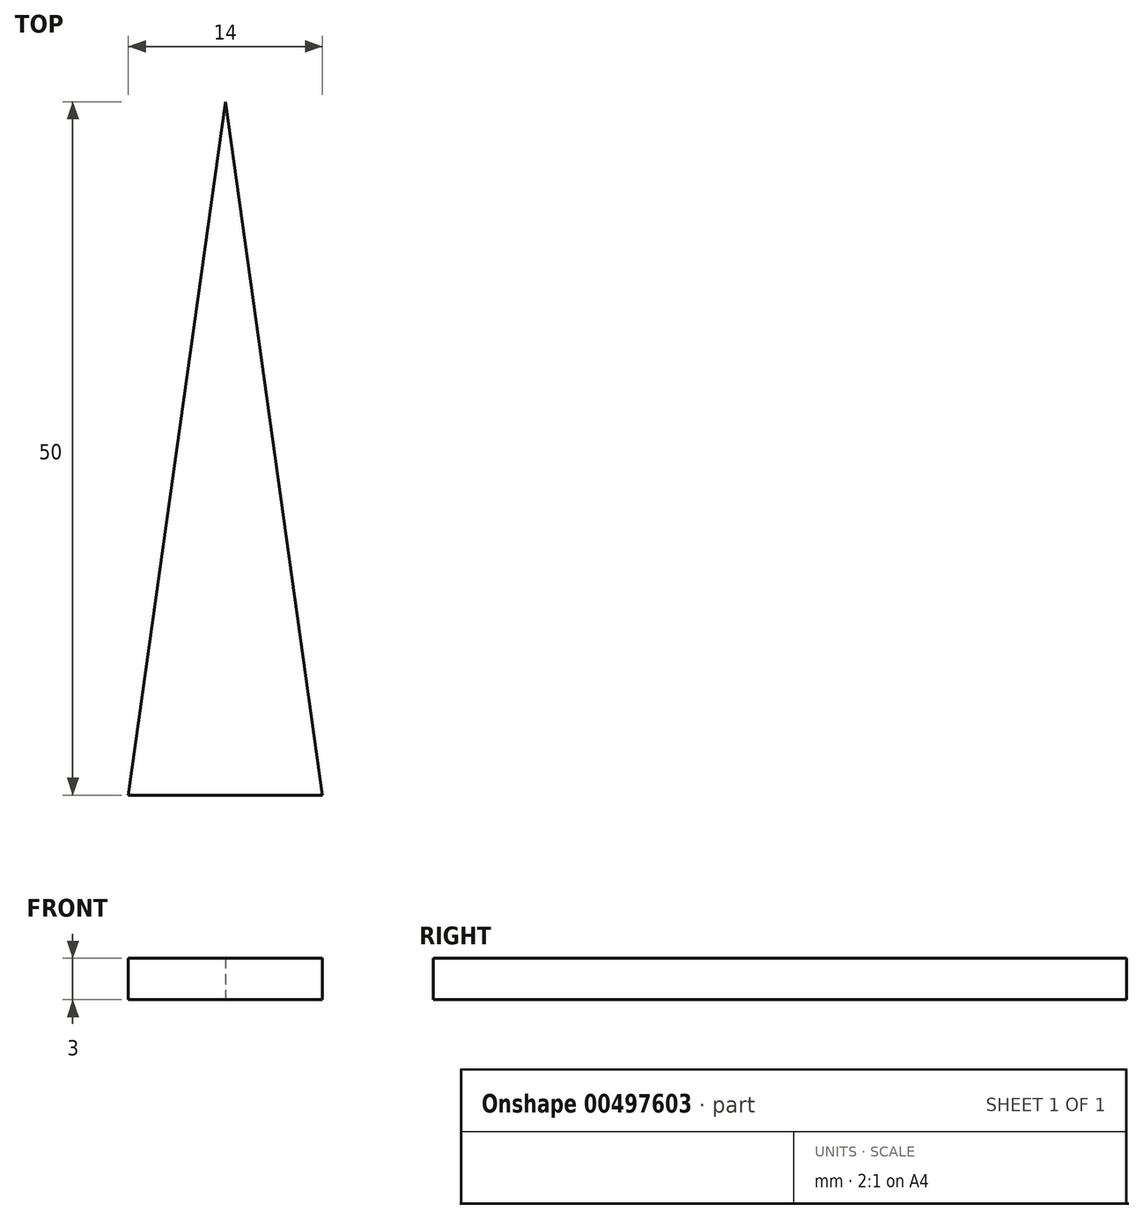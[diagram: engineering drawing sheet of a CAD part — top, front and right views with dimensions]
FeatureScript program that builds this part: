
annotation { "Feature Type Name" : "Feature", "Feature Type Description" : "" }
export const myFeature = defineFeature(function(context is Context, id is Id, definition is map)
    precondition{}
    {
        {
            var Q0;
            Q0=qCreatedBy(makeId("Top.planeOp"),FACE);
            var sketch = newSketch(context, id + "F0", { "sketchPlane" : qUnion([Q0])});
            skLineSegment(sketch, "E0", {"start": v(0, 0) * mm, "end": v(-7, -50) * mm});
            skLineSegment(sketch, "E1", {"start": v(-7, -50) * mm, "end": v(7, -50) * mm});
            skLineSegment(sketch, "E2", {"start": v(7, -50) * mm, "end": v(0, 0) * mm});
            skLineSegment(sketch, "E3", {"start": v(0, -50) * mm, "end": v(0, -45) * mm, "construction": true});
            skPoint(sketch, "E3.endSnap0", {"position": v(0, -50) * mm});
            skCircle(sketch, "E4", {"center": v(0, -45) * mm, "radius": 5 * mm});
            skSolve(sketch);
        }
        {
            var Q0;
            Q0 = qSketchRegion(id + "F0", true);
            extrude(context, id + "F1", {"entities" : qUnion([Q0]), "depth" : 3 * mm});
        }
    });
